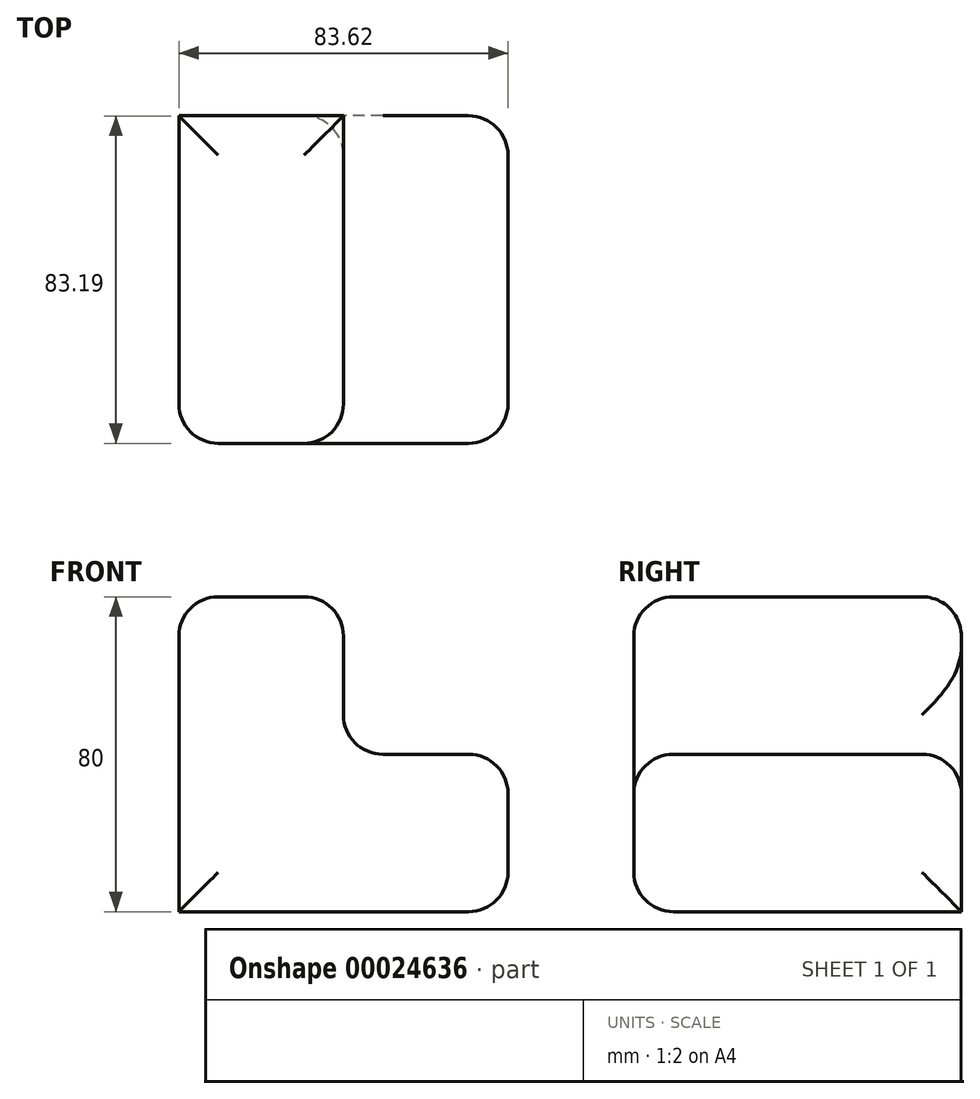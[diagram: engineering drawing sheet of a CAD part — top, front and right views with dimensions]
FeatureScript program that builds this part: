
annotation { "Feature Type Name" : "Feature", "Feature Type Description" : "" }
export const myFeature = defineFeature(function(context is Context, id is Id, definition is map)
    precondition{}
    {
        {
            var Q0;
            Q0=qCreatedBy(makeId("Top.planeOp"),FACE);
            var sketch = newSketch(context, id + "F0", { "sketchPlane" : qUnion([Q0])});
            skLineSegment(sketch, "E0.bottom", {"start": v(-59.13, -45.93) * mm, "end": v(24.5, -45.93) * mm});
            skLineSegment(sketch, "E0.top", {"start": v(-59.13, 37.26) * mm, "end": v(24.5, 37.26) * mm});
            skLineSegment(sketch, "E0.left", {"start": v(-59.13, -45.93) * mm, "end": v(-59.13, 37.26) * mm});
            skLineSegment(sketch, "E0.right", {"start": v(24.5, -45.93) * mm, "end": v(24.5, 37.26) * mm});
            skSolve(sketch);
        }
        {
            var Q0;
            Q0=makeQuery(id+"F0.imprint","IMPRINT",FACE,{"disambiguationData":[TD([[makeQuery(id+"F0.imprint","IMPRINT",EDGE,{"derivedFrom":sQuery(id+"F0.wireOp",EDGE,"E0.bottom")}),1.0]])]});
            extrude(context, id + "F1", {"entities" : qUnion([Q0]), "depth" : 40 * mm});
        }
        {
            var Q0;
            Q0=makeQuery(id+"F1.opExtrude","CAP_FACE",FACE,{"disambiguationData":[OSD([sQuery(id+"F0.wireOp",EDGE,"E0.bottom"),sQuery(id+"F0.wireOp",EDGE,"E0.top"),sQuery(id+"F0.wireOp",EDGE,"E0.left"),sQuery(id+"F0.wireOp",EDGE,"E0.right")])],"isStart":false});
            var sketch = newSketch(context, id + "F2", { "sketchPlane" : qUnion([Q0])});
            skLineSegment(sketch, "E1", {"start": v(-17.32, 37.26) * mm, "end": v(-17.32, -45.93) * mm});
            skSolve(sketch);
        }
        {
            var Q0;
            {var subQ1=sQuery(id+"F2.wireOp",EDGE,"E1");Q0=makeQuery(id+"F2.imprint","IMPRINT",FACE,{"disambiguationData":[TD([[makeQuery(id+"F2.imprint","IMPRINT",EDGE,{"derivedFrom":subQ1}),-1.0]])]});}
            extrude(context, id + "F3", {"entities" : qUnion([Q0]), "operationType" : NewBodyOperationType.ADD, "depth" : 40 * mm});
        }
        {
            var Q0;
            Q0=makeQuery(id+"F3.opExtrude","CAP_FACE",FACE,{"disambiguationData":[OSD([sQuery(id+"F0.wireOp",EDGE,"E0.bottom"),sQuery(id+"F0.wireOp",EDGE,"E0.top"),sQuery(id+"F0.wireOp",EDGE,"E0.left"),sQuery(id+"F2.wireOp",EDGE,"E1")])],"isStart":false});
            var Q1;
            Q1=makeQuery(id+"F1.opExtrude","CAP_FACE",FACE,{"disambiguationData":[OSD([sQuery(id+"F0.wireOp",EDGE,"E0.bottom"),sQuery(id+"F0.wireOp",EDGE,"E0.top"),sQuery(id+"F0.wireOp",EDGE,"E0.left"),sQuery(id+"F0.wireOp",EDGE,"E0.right")])],"isStart":false});
            var Q2;
            {var subQ0=sQuery(id+"F0.wireOp",EDGE,"E0.bottom");Q2=makeQuery(id+"F3.boolean.opBoolean","MERGE",FACE,{"derivedFrom":[makeQuery(id+"F1.opExtrude","SWEPT_FACE",FACE,{"disambiguationData":[OSD([subQ0])]}),makeQuery(id+"F3.opExtrude","SWEPT_FACE",FACE,{"disambiguationData":[OSD([subQ0])]})]});}
            var Q3;
            Q3=makeQuery(id+"F1.opExtrude","SWEPT_FACE",FACE,{"disambiguationData":[OSD([sQuery(id+"F0.wireOp",EDGE,"E0.right")])]});
            fillet(context, id + "F4", {"entities" : qUnion([Q0, Q1, Q2, Q3]), "radius" : 10 * mm, "tangentPropagation" : true, "allowEdgeOverflow" : false});
        }
    });
